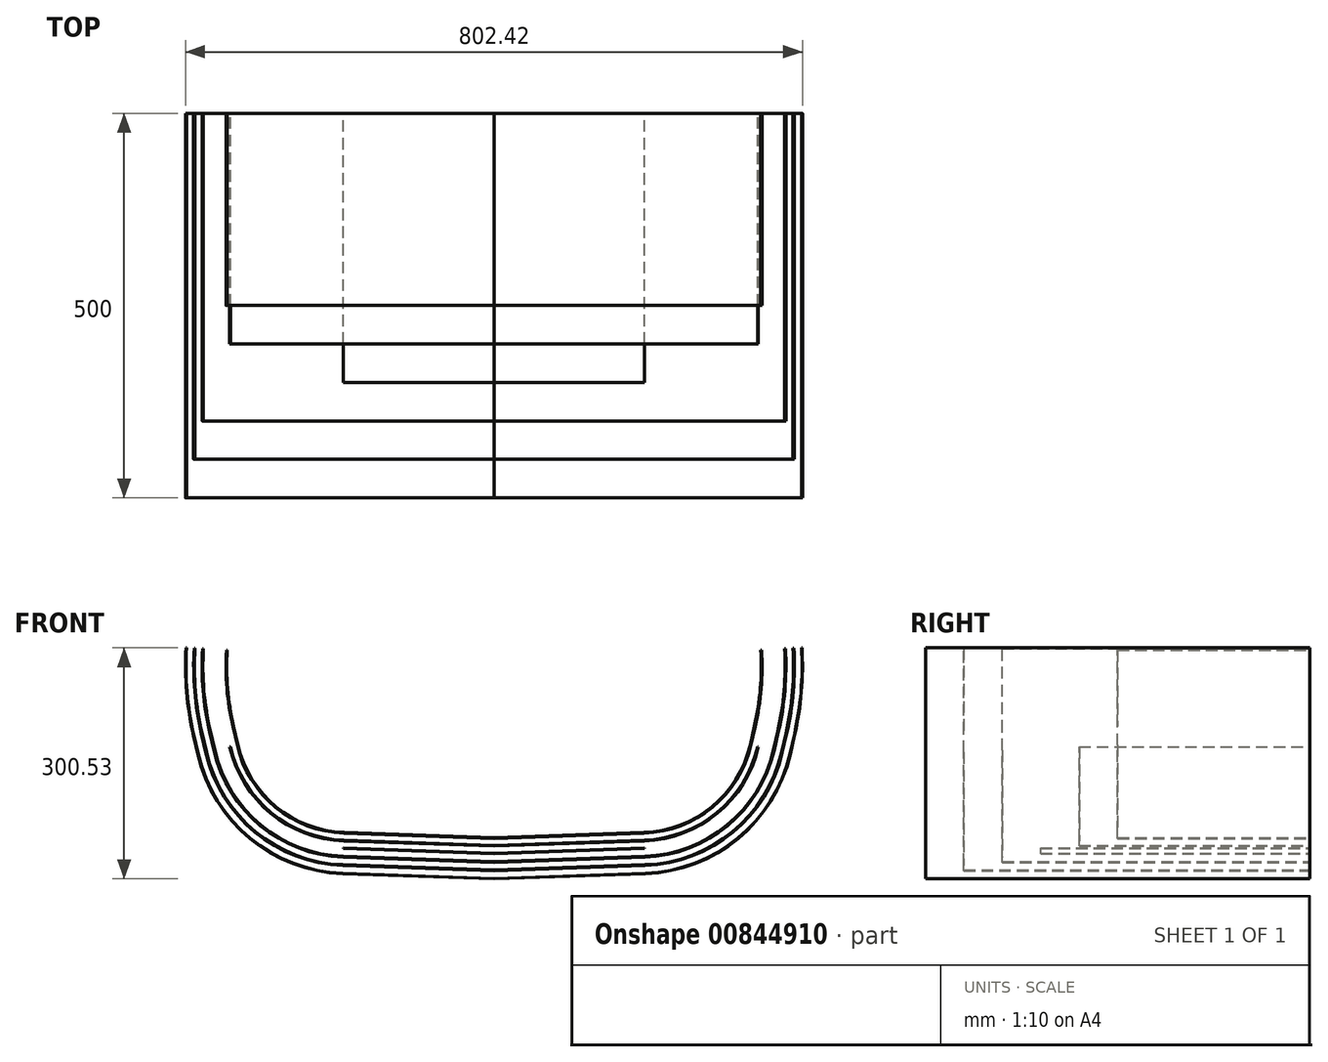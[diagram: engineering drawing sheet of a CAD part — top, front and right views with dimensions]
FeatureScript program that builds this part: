
annotation { "Feature Type Name" : "Feature", "Feature Type Description" : "" }
export const myFeature = defineFeature(function(context is Context, id is Id, definition is map)
    precondition{}
    {
        {
            var Q0;
            Q0=qCreatedBy(makeId("Front.planeOp"),FACE);
            var sketch = newSketch(context, id + "F0", { "sketchPlane" : qUnion([Q0])});
            skLineSegment(sketch, "E0", {"start": v(0, 0) * mm, "end": v(196.94, 6.88) * mm});
            skArc(sketch, "E1", {"start": v(196.94, 6.88) * mm, "mid": v(317.18, 52.43) * mm, "end": v(384.84, 161.77) * mm});
            skLineSegment(sketch, "E2", {"start": v(384.84, 161.77) * mm, "end": v(390.46, 186.12) * mm});
            skArc(sketch, "E3", {"start": v(390.46, 186.12) * mm, "mid": v(399.32, 242.72) * mm, "end": v(400, 300) * mm});
            skLineSegment(sketch, "E4", {"start": v(0, 0) * mm, "end": v(347.26, 0) * mm, "construction": true});
            skLineSegment(sketch, "E5", {"start": v(0, 0) * mm, "end": v(0, 338.6) * mm, "construction": true});
            skLineSegment(sketch, "E6.MirrorCS", {"start": v(0, 0) * mm, "end": v(-196.94, 6.88) * mm});
            skArc(sketch, "E7.MirrorCS", {"start": v(-196.94, 6.88) * mm, "mid": v(-317.18, 52.43) * mm, "end": v(-384.84, 161.77) * mm});
            skLineSegment(sketch, "E8.MirrorCS", {"start": v(-384.84, 161.77) * mm, "end": v(-390.46, 186.12) * mm});
            skArc(sketch, "E9.MirrorCS", {"start": v(-390.46, 186.12) * mm, "mid": v(-399.32, 242.72) * mm, "end": v(-400, 300) * mm});
            skArc(sketch, "E10.0", {"start": v(-390.95, 186.01) * mm, "mid": v(-399.82, 242.68) * mm, "end": v(-400.5, 300.03) * mm});
            skLineSegment(sketch, "E10.1", {"start": v(-385.33, 161.65) * mm, "end": v(-390.95, 186.01) * mm});
            skArc(sketch, "E10.2", {"start": v(-196.96, 6.38) * mm, "mid": v(-317.5, 52.04) * mm, "end": v(-385.33, 161.65) * mm});
            skLineSegment(sketch, "E10.3", {"start": v(0, -0.5) * mm, "end": v(-196.96, 6.38) * mm});
            skArc(sketch, "E10.4", {"start": v(390.95, 186.01) * mm, "mid": v(399.82, 242.68) * mm, "end": v(400.5, 300.03) * mm});
            skLineSegment(sketch, "E10.5", {"start": v(385.33, 161.65) * mm, "end": v(390.95, 186.01) * mm});
            skArc(sketch, "E10.6", {"start": v(196.96, 6.38) * mm, "mid": v(317.5, 52.04) * mm, "end": v(385.33, 161.65) * mm});
            skLineSegment(sketch, "E10.7", {"start": v(0, -0.5) * mm, "end": v(196.96, 6.38) * mm});
            skLineSegment(sketch, "E11", {"start": v(-400.5, 300.03) * mm, "end": v(-400, 300) * mm});
            skLineSegment(sketch, "E12", {"start": v(400.5, 300.03) * mm, "end": v(400, 300) * mm});
            skSolve(sketch);
        }
        {
            var Q0;
            Q0 = qSketchRegion(id + "F0", true);
            extrude(context, id + "F1", {"entities" : qUnion([Q0]), "depth" : 500 * mm, "offsetDistance" : 25 * mm});
        }
        {
            var Q0;
            Q0=qCreatedBy(makeId("Front.planeOp"),FACE);
            var sketch = newSketch(context, id + "F2", { "sketchPlane" : qUnion([Q0])});
            skArc(sketch, "E13.0", {"start": v(-390.46, 186.12) * mm, "mid": v(-399.32, 242.72) * mm, "end": v(-400, 300) * mm});
            skLineSegment(sketch, "E14.0", {"start": v(-384.84, 161.77) * mm, "end": v(-390.46, 186.12) * mm});
            skArc(sketch, "E15.0", {"start": v(-196.94, 6.88) * mm, "mid": v(-317.18, 52.43) * mm, "end": v(-384.84, 161.77) * mm});
            skLineSegment(sketch, "E16.0", {"start": v(0, 0) * mm, "end": v(-196.94, 6.88) * mm});
            skArc(sketch, "E17.0", {"start": v(-380.72, 188.37) * mm, "mid": v(-389.35, 243.55) * mm, "end": v(-390.02, 299.4) * mm});
            skLineSegment(sketch, "E17.1", {"start": v(-375.1, 164.01) * mm, "end": v(-380.72, 188.37) * mm});
            skArc(sketch, "E17.2", {"start": v(-196.6, 16.87) * mm, "mid": v(-310.82, 60.15) * mm, "end": v(-375.1, 164.01) * mm});
            skLineSegment(sketch, "E17.3", {"start": v(0, 10) * mm, "end": v(-196.6, 16.87) * mm});
            skLineSegment(sketch, "E18", {"start": v(0, 0) * mm, "end": v(0, 258.23) * mm, "construction": true});
            skArc(sketch, "E19.0", {"start": v(-379.74, 188.6) * mm, "mid": v(-388.36, 243.64) * mm, "end": v(-389.02, 299.34) * mm});
            skLineSegment(sketch, "E19.1", {"start": v(-374.12, 164.24) * mm, "end": v(-379.74, 188.6) * mm});
            skArc(sketch, "E19.2", {"start": v(-196.56, 17.87) * mm, "mid": v(-310.18, 60.92) * mm, "end": v(-374.12, 164.24) * mm});
            skLineSegment(sketch, "E19.3", {"start": v(0, 11) * mm, "end": v(-196.56, 17.87) * mm});
            skLineSegment(sketch, "E20", {"start": v(-390.02, 299.4) * mm, "end": v(-389.02, 299.34) * mm});
            skLineSegment(sketch, "E21.MirrorCS", {"start": v(0, 10) * mm, "end": v(196.6, 16.87) * mm});
            skLineSegment(sketch, "E22.MirrorCS", {"start": v(0, 11) * mm, "end": v(196.56, 17.87) * mm});
            skArc(sketch, "E23.MirrorCS", {"start": v(196.6, 16.87) * mm, "mid": v(310.82, 60.15) * mm, "end": v(375.1, 164.01) * mm});
            skArc(sketch, "E24.MirrorCS", {"start": v(196.56, 17.87) * mm, "mid": v(310.18, 60.92) * mm, "end": v(374.12, 164.24) * mm});
            skLineSegment(sketch, "E25.MirrorCS", {"start": v(375.1, 164.01) * mm, "end": v(380.72, 188.37) * mm});
            skLineSegment(sketch, "E26.MirrorCS", {"start": v(374.12, 164.24) * mm, "end": v(379.74, 188.6) * mm});
            skArc(sketch, "E27.MirrorCS", {"start": v(380.72, 188.37) * mm, "mid": v(389.35, 243.55) * mm, "end": v(390.02, 299.4) * mm});
            skArc(sketch, "E28.MirrorCS", {"start": v(379.74, 188.6) * mm, "mid": v(388.36, 243.64) * mm, "end": v(389.02, 299.34) * mm});
            skLineSegment(sketch, "E29.MirrorCS", {"start": v(390.02, 299.4) * mm, "end": v(389.02, 299.34) * mm});
            skSolve(sketch);
        }
        {
            var Q0;
            Q0 = qSketchRegion(id + "F2", true);
            extrude(context, id + "F3", {"entities" : qUnion([Q0]), "depth" : 450 * mm, "offsetDistance" : 25 * mm});
        }
        {
            var Q0;
            Q0=qCreatedBy(makeId("Front.planeOp"),FACE);
            var sketch = newSketch(context, id + "F4", { "sketchPlane" : qUnion([Q0])});
            skArc(sketch, "E30.0", {"start": v(-379.74, 188.6) * mm, "mid": v(-388.36, 243.64) * mm, "end": v(-389.02, 299.34) * mm});
            skLineSegment(sketch, "E31.0", {"start": v(-374.12, 164.24) * mm, "end": v(-379.74, 188.6) * mm});
            skArc(sketch, "E32.0", {"start": v(-196.56, 17.87) * mm, "mid": v(-310.18, 60.92) * mm, "end": v(-374.12, 164.24) * mm});
            skLineSegment(sketch, "E33.0", {"start": v(0, 11) * mm, "end": v(-196.56, 17.87) * mm});
            skArc(sketch, "E34.0", {"start": v(-370, 190.85) * mm, "mid": v(-378.4, 244.47) * mm, "end": v(-379.04, 298.75) * mm});
            skLineSegment(sketch, "E34.1", {"start": v(-364.38, 166.49) * mm, "end": v(-370, 190.85) * mm});
            skArc(sketch, "E34.2", {"start": v(-196.21, 27.86) * mm, "mid": v(-303.82, 68.63) * mm, "end": v(-364.38, 166.49) * mm});
            skLineSegment(sketch, "E34.3", {"start": v(0, 21.01) * mm, "end": v(-196.21, 27.86) * mm});
            skArc(sketch, "E35.0", {"start": v(-369.03, 191.07) * mm, "mid": v(-377.4, 244.56) * mm, "end": v(-378.04, 298.69) * mm});
            skLineSegment(sketch, "E35.1", {"start": v(-363.4, 166.71) * mm, "end": v(-369.03, 191.07) * mm});
            skArc(sketch, "E35.2", {"start": v(-196.18, 28.86) * mm, "mid": v(-303.19, 69.4) * mm, "end": v(-363.4, 166.71) * mm});
            skLineSegment(sketch, "E35.3", {"start": v(0, 22.01) * mm, "end": v(-196.18, 28.86) * mm});
            skLineSegment(sketch, "E36", {"start": v(-379.04, 298.75) * mm, "end": v(-378.04, 298.69) * mm});
            skLineSegment(sketch, "E37", {"start": v(0, 0) * mm, "end": v(0, 60.12) * mm, "construction": true});
            skArc(sketch, "E38.MirrorCS", {"start": v(196.21, 27.86) * mm, "mid": v(303.82, 68.63) * mm, "end": v(364.38, 166.49) * mm});
            skLineSegment(sketch, "E39.MirrorCS", {"start": v(0, 21.01) * mm, "end": v(196.21, 27.86) * mm});
            skLineSegment(sketch, "E40.MirrorCS", {"start": v(0, 22.01) * mm, "end": v(196.18, 28.86) * mm});
            skArc(sketch, "E41.MirrorCS", {"start": v(196.18, 28.86) * mm, "mid": v(303.19, 69.4) * mm, "end": v(363.4, 166.71) * mm});
            skArc(sketch, "E42.MirrorCS", {"start": v(370, 190.85) * mm, "mid": v(378.4, 244.47) * mm, "end": v(379.04, 298.75) * mm});
            skLineSegment(sketch, "E43.MirrorCS", {"start": v(364.38, 166.49) * mm, "end": v(370, 190.85) * mm});
            skLineSegment(sketch, "E44.MirrorCS", {"start": v(363.4, 166.71) * mm, "end": v(369.03, 191.07) * mm});
            skArc(sketch, "E45.MirrorCS", {"start": v(369.03, 191.07) * mm, "mid": v(377.4, 244.56) * mm, "end": v(378.04, 298.69) * mm});
            skLineSegment(sketch, "E46.MirrorCS", {"start": v(379.04, 298.75) * mm, "end": v(378.04, 298.69) * mm});
            skSolve(sketch);
        }
        {
            var Q0;
            Q0 = qSketchRegion(id + "F4", true);
            extrude(context, id + "F5", {"entities" : qUnion([Q0]), "depth" : 400 * mm, "offsetDistance" : 25 * mm});
        }
        {
            var Q0;
            Q0=qCreatedBy(makeId("Front.planeOp"),FACE);
            var sketch = newSketch(context, id + "F6", { "sketchPlane" : qUnion([Q0])});
            skArc(sketch, "E47.0", {"start": v(-369.03, 191.07) * mm, "mid": v(-377.4, 244.56) * mm, "end": v(-378.04, 298.69) * mm});
            skArc(sketch, "E48.0", {"start": v(-196.18, 28.86) * mm, "mid": v(-303.19, 69.4) * mm, "end": v(-363.4, 166.71) * mm});
            skLineSegment(sketch, "E49.0", {"start": v(0, 22.01) * mm, "end": v(-196.18, 28.86) * mm});
            skLineSegment(sketch, "E50.3", {"start": v(0, 32.02) * mm, "end": v(-195.83, 38.86) * mm});
            skLineSegment(sketch, "E51.3", {"start": v(0, 33.02) * mm, "end": v(-195.8, 39.86) * mm});
            skLineSegment(sketch, "E52", {"start": v(-195.83, 38.86) * mm, "end": v(-195.8, 39.86) * mm});
            skLineSegment(sketch, "E53", {"start": v(0, 22.01) * mm, "end": v(0, 33.02) * mm, "construction": true});
            skLineSegment(sketch, "E54.MirrorCS", {"start": v(0, 32.02) * mm, "end": v(195.83, 38.86) * mm});
            skLineSegment(sketch, "E55.MirrorCS", {"start": v(0, 33.02) * mm, "end": v(195.8, 39.86) * mm});
            skLineSegment(sketch, "E56.MirrorCS", {"start": v(195.83, 38.86) * mm, "end": v(195.8, 39.86) * mm});
            skSolve(sketch);
        }
        {
            var Q0;
            Q0 = qSketchRegion(id + "F6", true);
            extrude(context, id + "F7", {"entities" : qUnion([Q0]), "depth" : 350 * mm, "offsetDistance" : 25 * mm});
        }
        {
            var Q0;
            Q0=qCreatedBy(makeId("Front.planeOp"),FACE);
            var sketch = newSketch(context, id + "F8", { "sketchPlane" : qUnion([Q0])});
            skArc(sketch, "E57.0", {"start": v(-196.18, 28.86) * mm, "mid": v(-303.19, 69.4) * mm, "end": v(-363.4, 166.71) * mm});
            skLineSegment(sketch, "E58.0", {"start": v(0, 22.01) * mm, "end": v(-196.18, 28.86) * mm});
            skArc(sketch, "E59.0", {"start": v(-195.48, 48.85) * mm, "mid": v(-290.46, 84.84) * mm, "end": v(-343.92, 171.21) * mm});
            skLineSegment(sketch, "E59.1", {"start": v(0, 42.03) * mm, "end": v(-195.48, 48.85) * mm});
            skArc(sketch, "E60.0", {"start": v(-195.44, 49.85) * mm, "mid": v(-289.83, 85.61) * mm, "end": v(-342.94, 171.44) * mm});
            skLineSegment(sketch, "E60.1", {"start": v(0, 43.03) * mm, "end": v(-195.44, 49.85) * mm});
            skLineSegment(sketch, "E61", {"start": v(-343.92, 171.21) * mm, "end": v(-342.94, 171.44) * mm});
            skLineSegment(sketch, "E62", {"start": v(0, 1.53) * mm, "end": v(0, 91.07) * mm, "construction": true});
            skLineSegment(sketch, "E63.MirrorCS", {"start": v(0, 43.03) * mm, "end": v(195.44, 49.85) * mm});
            skArc(sketch, "E64.MirrorCS", {"start": v(195.48, 48.85) * mm, "mid": v(290.46, 84.84) * mm, "end": v(343.92, 171.21) * mm});
            skLineSegment(sketch, "E65.MirrorCS", {"start": v(0, 42.03) * mm, "end": v(195.48, 48.85) * mm});
            skArc(sketch, "E66.MirrorCS", {"start": v(195.44, 49.85) * mm, "mid": v(289.83, 85.61) * mm, "end": v(342.94, 171.44) * mm});
            skLineSegment(sketch, "E67.MirrorCS", {"start": v(343.92, 171.21) * mm, "end": v(342.94, 171.44) * mm});
            skSolve(sketch);
        }
        {
            var Q0;
            Q0 = qSketchRegion(id + "F8", true);
            extrude(context, id + "F9", {"entities" : qUnion([Q0]), "depth" : 300 * mm, "offsetDistance" : 25 * mm});
        }
        {
            var Q0;
            Q0=qCreatedBy(makeId("Front.planeOp"),FACE);
            var sketch = newSketch(context, id + "F10", { "sketchPlane" : qUnion([Q0])});
            skArc(sketch, "E68.0", {"start": v(-369.03, 191.07) * mm, "mid": v(-377.4, 244.56) * mm, "end": v(-378.04, 298.69) * mm});
            skLineSegment(sketch, "E69.0", {"start": v(-363.4, 166.71) * mm, "end": v(-369.03, 191.07) * mm});
            skArc(sketch, "E70.0", {"start": v(-196.18, 28.86) * mm, "mid": v(-303.19, 69.4) * mm, "end": v(-363.4, 166.71) * mm});
            skLineSegment(sketch, "E71.0", {"start": v(0, 22.01) * mm, "end": v(-196.18, 28.86) * mm});
            skArc(sketch, "E72.0", {"start": v(-339.8, 197.82) * mm, "mid": v(-347.5, 247.06) * mm, "end": v(-348.1, 296.9) * mm});
            skLineSegment(sketch, "E72.1", {"start": v(-334.17, 173.46) * mm, "end": v(-339.8, 197.82) * mm});
            skArc(sketch, "E72.2", {"start": v(-195.13, 58.85) * mm, "mid": v(-284.1, 92.56) * mm, "end": v(-334.17, 173.46) * mm});
            skLineSegment(sketch, "E72.3", {"start": v(0, 52.03) * mm, "end": v(-195.13, 58.85) * mm});
            skArc(sketch, "E73.0", {"start": v(-338.82, 198.05) * mm, "mid": v(-346.5, 247.14) * mm, "end": v(-347.1, 296.83) * mm});
            skLineSegment(sketch, "E73.1", {"start": v(-333.2, 173.69) * mm, "end": v(-338.82, 198.05) * mm});
            skArc(sketch, "E73.2", {"start": v(-195.1, 59.85) * mm, "mid": v(-283.47, 93.33) * mm, "end": v(-333.2, 173.69) * mm});
            skLineSegment(sketch, "E73.3", {"start": v(0, 53.03) * mm, "end": v(-195.1, 59.85) * mm});
            skLineSegment(sketch, "E74", {"start": v(-348.1, 296.9) * mm, "end": v(-347.1, 296.83) * mm});
            skLineSegment(sketch, "E75", {"start": v(0, 0) * mm, "end": v(0, 128.95) * mm, "construction": true});
            skArc(sketch, "E76.MirrorCS", {"start": v(195.13, 58.85) * mm, "mid": v(284.1, 92.56) * mm, "end": v(334.17, 173.46) * mm});
            skLineSegment(sketch, "E77.MirrorCS", {"start": v(0, 53.03) * mm, "end": v(195.1, 59.85) * mm});
            skLineSegment(sketch, "E78.MirrorCS", {"start": v(0, 52.03) * mm, "end": v(195.13, 58.85) * mm});
            skArc(sketch, "E79.MirrorCS", {"start": v(195.1, 59.85) * mm, "mid": v(283.47, 93.33) * mm, "end": v(333.2, 173.69) * mm});
            skArc(sketch, "E80.MirrorCS", {"start": v(338.82, 198.05) * mm, "mid": v(346.5, 247.14) * mm, "end": v(347.1, 296.83) * mm});
            skArc(sketch, "E81.MirrorCS", {"start": v(339.8, 197.82) * mm, "mid": v(347.5, 247.06) * mm, "end": v(348.1, 296.9) * mm});
            skLineSegment(sketch, "E82.MirrorCS", {"start": v(333.2, 173.69) * mm, "end": v(338.82, 198.05) * mm});
            skLineSegment(sketch, "E83.MirrorCS", {"start": v(334.17, 173.46) * mm, "end": v(339.8, 197.82) * mm});
            skLineSegment(sketch, "E84.MirrorCS", {"start": v(348.1, 296.9) * mm, "end": v(347.1, 296.83) * mm});
            skSolve(sketch);
        }
        {
            var Q0;
            Q0 = qSketchRegion(id + "F10", true);
            extrude(context, id + "F11", {"entities" : qUnion([Q0]), "depth" : 250 * mm, "offsetDistance" : 25 * mm});
        }
    });
